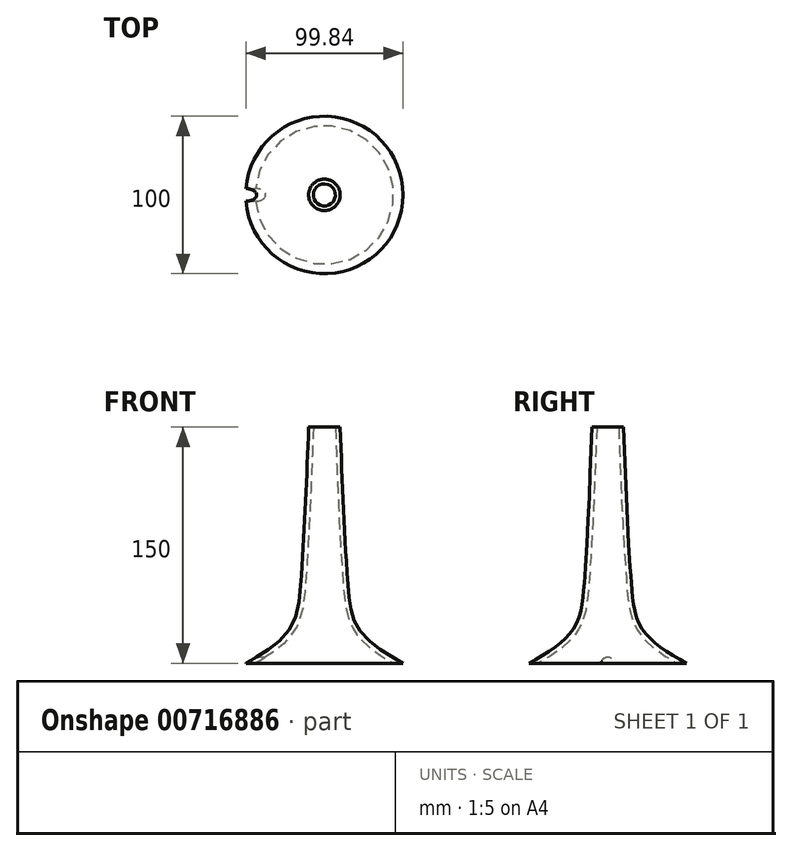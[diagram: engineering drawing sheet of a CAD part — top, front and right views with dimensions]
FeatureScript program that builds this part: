
annotation { "Feature Type Name" : "Feature", "Feature Type Description" : "" }
export const myFeature = defineFeature(function(context is Context, id is Id, definition is map)
    precondition{}
    {
        {
            var Q0;
            Q0=qCreatedBy(makeId("Top.planeOp"),FACE);
            var sketch = newSketch(context, id + "F0", { "sketchPlane" : qUnion([Q0])});
            skCircle(sketch, "E0", {"center": v(0, 0) * mm, "radius": 50 * mm});
            skSolve(sketch);
        }
        {
            var Q0;
            Q0=qCreatedBy(makeId("Top.planeOp"),FACE);
            cPlane(context, id + "F1", {"entities" : qUnion([Q0]), "cplaneType" : CPlaneType.OFFSET, "offset" : 25 * mm, "width" : 150 * mm, "height" : 150 * mm});
        }
        {
            var Q0;
            Q0=qCreatedBy(makeId("Top.planeOp"),FACE);
            cPlane(context, id + "F2", {"entities" : qUnion([Q0]), "cplaneType" : CPlaneType.OFFSET, "offset" : 150 * mm, "width" : 150 * mm, "height" : 150 * mm});
        }
        {
            var Q0;
            Q0=qCreatedBy(id+"F1.planeOp",FACE);
            var sketch = newSketch(context, id + "F3", { "sketchPlane" : qUnion([Q0])});
            skCircle(sketch, "E1", {"center": v(0, 0) * mm, "radius": 20 * mm});
            skSolve(sketch);
        }
        {
            var Q0;
            Q0=qCreatedBy(id+"F2.planeOp",FACE);
            var sketch = newSketch(context, id + "F4", { "sketchPlane" : qUnion([Q0])});
            skCircle(sketch, "E2", {"center": v(0, 0) * mm, "radius": 10 * mm});
            skSolve(sketch);
        }
        {
            var Q0;
            Q0=qCreatedBy(makeId("Top.planeOp"),FACE);
            cPlane(context, id + "F5", {"entities" : qUnion([Q0]), "cplaneType" : CPlaneType.OFFSET, "offset" : 50 * mm, "width" : 150 * mm, "height" : 150 * mm});
        }
        {
            var Q0;
            Q0=qCreatedBy(id+"F5.planeOp",FACE);
            var sketch = newSketch(context, id + "F6", { "sketchPlane" : qUnion([Q0])});
            skCircle(sketch, "E3", {"center": v(0, 0) * mm, "radius": 15 * mm});
            skSolve(sketch);
        }
        {
            var Q0;
            Q0=makeQuery(id+"F0.imprint","IMPRINT",FACE,{"disambiguationData":[TD([[makeQuery(id+"F0.imprint","IMPRINT",EDGE,{"derivedFrom":sQuery(id+"F0.wireOp",EDGE,"E0")}),1.0]])]});
            var Q1;
            Q1=makeQuery(id+"F3.imprint","IMPRINT",FACE,{"disambiguationData":[TD([[makeQuery(id+"F3.imprint","IMPRINT",EDGE,{"derivedFrom":sQuery(id+"F3.wireOp",EDGE,"E1")}),1.0]])]});
            var Q2;
            Q2=makeQuery(id+"F6.imprint","IMPRINT",FACE,{"disambiguationData":[TD([[makeQuery(id+"F6.imprint","IMPRINT",EDGE,{"derivedFrom":sQuery(id+"F6.wireOp",EDGE,"E3")}),1.0]])]});
            var Q3;
            Q3=makeQuery(id+"F4.imprint","IMPRINT",FACE,{"disambiguationData":[TD([[makeQuery(id+"F4.imprint","IMPRINT",EDGE,{"derivedFrom":sQuery(id+"F4.wireOp",EDGE,"E2")}),1.0]])]});
            loft(context, id + "F7", {"sheetProfilesArray" : [{ "sheetProfileEntities" : qUnion([Q0]) }, { "sheetProfileEntities" : qUnion([Q1]) }, { "sheetProfileEntities" : qUnion([Q2]) }, { "sheetProfileEntities" : qUnion([Q3]) }]});
        }
        {
            var Q0;
            Q0=makeQuery(id+"F7.opLoft","CAP_FACE",FACE,{"disambiguationData":[OSD([makeQuery(id+"F0.imprint","IMPRINT",FACE,{"disambiguationData":[TD([[makeQuery(id+"F0.imprint","IMPRINT",EDGE,{"derivedFrom":sQuery(id+"F0.wireOp",EDGE,"E0")}),1.0]])]})])],"isStart":true});
            var Q1;
            Q1=makeQuery(id+"F7.opLoft","CAP_FACE",FACE,{"disambiguationData":[OSD([makeQuery(id+"F4.imprint","IMPRINT",FACE,{"disambiguationData":[TD([[makeQuery(id+"F4.imprint","IMPRINT",EDGE,{"derivedFrom":sQuery(id+"F4.wireOp",EDGE,"E2")}),1.0]])]})])],"isStart":true});
            shell(context, id + "F8", {"entities" : qUnion([Q0, Q1]), "thickness" : 3 * mm});
        }
        {
            var Q0;
            Q0=qCreatedBy(makeId("Right.planeOp"),FACE);
            var sketch = newSketch(context, id + "F9", { "sketchPlane" : qUnion([Q0])});
            skCircle(sketch, "E4", {"center": v(0, 0) * mm, "radius": 4 * mm});
            skSolve(sketch);
        }
        {
            var Q0;
            Q0=makeQuery(id+"F9.imprint","IMPRINT",FACE,{"disambiguationData":[TD([[makeQuery(id+"F9.imprint","IMPRINT",EDGE,{"derivedFrom":sQuery(id+"F9.wireOp",EDGE,"E4")}),1.0]])]});
            var Q1;
            Q1=sQuery(id+"F9.wireOp",EDGE,"E4");
            extrude(context, id + "F10", {"entities" : qUnion([Q0]), "operationType" : NewBodyOperationType.REMOVE, "surfaceEntities" : qUnion([Q1]), "oppositeDirection" : true, "depth" : 60 * mm, "offsetDistance" : 25 * mm});
        }
    });
